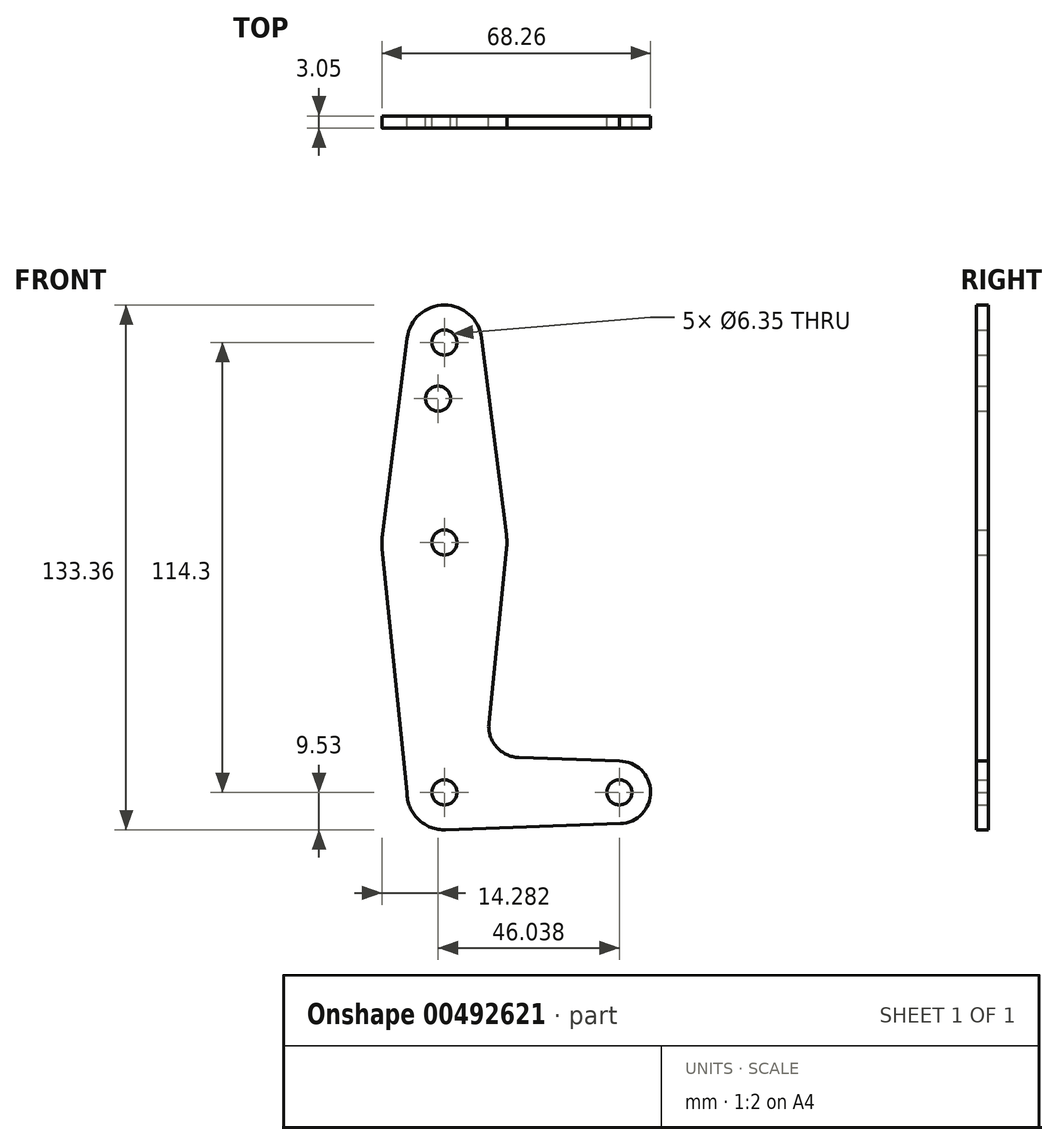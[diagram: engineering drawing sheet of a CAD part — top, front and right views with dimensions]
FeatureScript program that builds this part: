
annotation { "Feature Type Name" : "Feature", "Feature Type Description" : "" }
export const myFeature = defineFeature(function(context is Context, id is Id, definition is map)
    precondition{}
    {
        {
            var Q0;
            Q0=qCreatedBy(makeId("Front.planeOp"),FACE);
            var sketch = newSketch(context, id + "F0", { "sketchPlane" : qUnion([Q0])});
            skLineSegment(sketch, "E0", {"start": v(0, 114.3) * mm, "end": v(0, 0) * mm, "construction": true});
            skLineSegment(sketch, "E1", {"start": v(0, 0) * mm, "end": v(44.45, 0) * mm, "construction": true});
            skCircle(sketch, "E2", {"center": v(0, 114.3) * mm, "radius": 9.53 * mm});
            skCircle(sketch, "E3", {"center": v(0, 0) * mm, "radius": 9.53 * mm});
            skCircle(sketch, "E4", {"center": v(0, 63.5) * mm, "radius": 15.88 * mm});
            skCircle(sketch, "E5", {"center": v(44.45, 0) * mm, "radius": 7.94 * mm});
            skLineSegment(sketch, "E6", {"start": v(9.45, 115.5) * mm, "end": v(15.75, 65.48) * mm});
            skLineSegment(sketch, "E7", {"start": v(-9.45, 115.5) * mm, "end": v(-15.75, 65.48) * mm});
            skLineSegment(sketch, "E8", {"start": v(44.45, 7.94) * mm, "end": v(18.93, 8.85) * mm});
            skLineSegment(sketch, "E9", {"start": v(44.73, -7.93) * mm, "end": v(0.34, -9.52) * mm});
            skCircle(sketch, "E10", {"center": v(0, 114.3) * mm, "radius": 3.18 * mm});
            skCircle(sketch, "E11", {"center": v(0, 63.5) * mm, "radius": 3.18 * mm});
            skCircle(sketch, "E12", {"center": v(0, 0) * mm, "radius": 3.18 * mm});
            skCircle(sketch, "E13", {"center": v(44.45, 0) * mm, "radius": 3.18 * mm});
            skCircle(sketch, "E14", {"center": v(-1.59, 100.03) * mm, "radius": 3.18 * mm});
            skLineSegment(sketch, "E15", {"start": v(15.8, 61.9) * mm, "end": v(11.3, 17.6) * mm});
            skLineSegment(sketch, "E16", {"start": v(-15.8, 61.9) * mm, "end": v(-9.53, 0) * mm});
            skArc(sketch, "E17.filletArc", {"start": v(11.3, 17.6) * mm, "mid": v(13.22, 11.57) * mm, "end": v(18.93, 8.85) * mm});
            skSolve(sketch);
        }
        {
            var Q0;
            Q0 = qSketchRegion(id + "F0", true);
            extrude(context, id + "F1", {"entities" : qUnion([Q0]), "depth" : 3.05 * mm});
        }
    });
